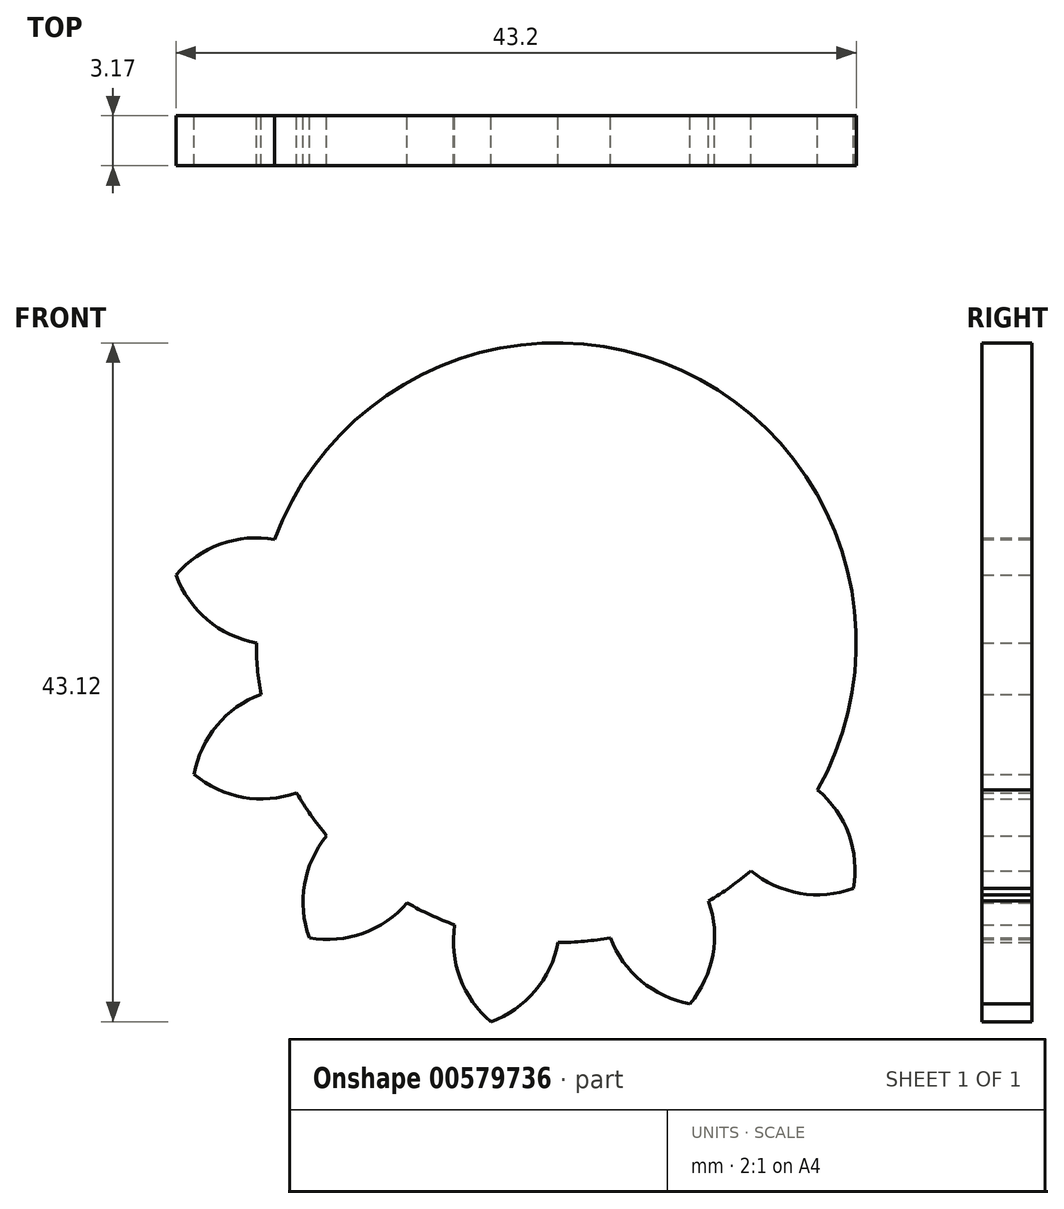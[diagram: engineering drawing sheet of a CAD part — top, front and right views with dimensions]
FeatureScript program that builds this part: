
annotation { "Feature Type Name" : "Feature", "Feature Type Description" : "" }
export const myFeature = defineFeature(function(context is Context, id is Id, definition is map)
    precondition{}
    {
        {
            var Q0;
            Q0=qCreatedBy(makeId("Front.planeOp"),FACE);
            var sketch = newSketch(context, id + "F0", { "sketchPlane" : qUnion([Q0])});
            skCircle(sketch, "E0", {"center": v(0, 0) * mm, "radius": 19.05 * mm});
            skArc(sketch, "E1", {"start": v(-17.89, 6.56) * mm, "mid": v(-21.32, 6.26) * mm, "end": v(-24.15, 4.29) * mm});
            skArc(sketch, "E2", {"start": v(-24.15, 4.29) * mm, "mid": v(-22.17, 1.46) * mm, "end": v(-19.05, 0) * mm});
            skArc(sketch, "E3.1.0", {"start": v(-18.71, -3.26) * mm, "mid": v(-21.54, -5.24) * mm, "end": v(-23, -8.36) * mm});
            skArc(sketch, "E3.1.1", {"start": v(-23, -8.36) * mm, "mid": v(-19.88, -9.82) * mm, "end": v(-16.44, -9.52) * mm});
            skArc(sketch, "E3.2.0", {"start": v(-14.52, -12.18) * mm, "mid": v(-15.98, -15.3) * mm, "end": v(-15.69, -18.74) * mm});
            skArc(sketch, "E3.2.1", {"start": v(-15.69, -18.74) * mm, "mid": v(-12.25, -18.44) * mm, "end": v(-9.42, -16.47) * mm});
            skArc(sketch, "E3.3.0", {"start": v(-6.43, -17.81) * mm, "mid": v(-6.13, -21.25) * mm, "end": v(-4.16, -24.07) * mm});
            skArc(sketch, "E3.3.1", {"start": v(-4.16, -24.07) * mm, "mid": v(-1.33, -22.1) * mm, "end": v(0.13, -18.98) * mm});
            skArc(sketch, "E3.4.0", {"start": v(3.39, -18.64) * mm, "mid": v(5.36, -21.47) * mm, "end": v(8.49, -22.93) * mm});
            skArc(sketch, "E3.4.1", {"start": v(8.49, -22.93) * mm, "mid": v(9.95, -19.8) * mm, "end": v(9.65, -16.37) * mm});
            skArc(sketch, "E3.5.0", {"start": v(12.3, -14.45) * mm, "mid": v(15.43, -15.9) * mm, "end": v(18.87, -15.61) * mm});
            skArc(sketch, "E3.5.1", {"start": v(18.87, -15.61) * mm, "mid": v(18.57, -12.18) * mm, "end": v(16.6, -9.35) * mm});
            skArc(sketch, "E3.6.0", {"start": v(17.94, -6.36) * mm, "mid": v(21.37, -6.06) * mm, "end": v(24.2, -4.09) * mm});
            skArc(sketch, "E3.6.1", {"start": v(24.2, -4.09) * mm, "mid": v(22.23, -1.26) * mm, "end": v(19.1, 0.2) * mm});
            skArc(sketch, "E3.7.0", {"start": v(18.77, 3.46) * mm, "mid": v(21.6, 5.44) * mm, "end": v(23.06, 8.56) * mm});
            skArc(sketch, "E3.7.1", {"start": v(23.06, 8.56) * mm, "mid": v(19.93, 10.02) * mm, "end": v(16.5, 9.73) * mm});
            skArc(sketch, "E3.8.0", {"start": v(14.58, 12.38) * mm, "mid": v(16.04, 15.5) * mm, "end": v(15.74, 18.94) * mm});
            skArc(sketch, "E3.8.1", {"start": v(15.74, 18.94) * mm, "mid": v(12.3, 18.65) * mm, "end": v(9.48, 16.67) * mm});
            skArc(sketch, "E3.9.0", {"start": v(6.48, 18.01) * mm, "mid": v(6.19, 21.45) * mm, "end": v(4.21, 24.28) * mm});
            skArc(sketch, "E3.9.1", {"start": v(4.21, 24.28) * mm, "mid": v(1.39, 22.3) * mm, "end": v(-0.07, 19.18) * mm});
            skArc(sketch, "E3.10.0", {"start": v(-3.34, 18.84) * mm, "mid": v(-5.31, 21.67) * mm, "end": v(-8.43, 23.13) * mm});
            skArc(sketch, "E3.10.1", {"start": v(-8.43, 23.13) * mm, "mid": v(-9.9, 20) * mm, "end": v(-9.6, 16.57) * mm});
            skArc(sketch, "E3.11.0", {"start": v(-12.26, 14.65) * mm, "mid": v(-15.38, 16.11) * mm, "end": v(-18.82, 15.81) * mm});
            skArc(sketch, "E3.11.1", {"start": v(-18.82, 15.81) * mm, "mid": v(-18.52, 12.38) * mm, "end": v(-16.54, 9.55) * mm});
            skPoint(sketch, "E3.center", {"position": v(0.03, 0.1) * mm});
            skSolve(sketch);
        }
        {
            var Q0;
            {var subQ0=sQuery(id+"F0.wireOp",EDGE,"E0");var subQ15=makeQuery(id+"F0.imprint","INTERSECT",VERTEX,{"derivedFrom":[subQ0,sQuery(id+"F0.wireOp",EDGE,"E3.6.1")]});Q0=makeQuery(id+"F0.imprint","IMPRINT",FACE,{"disambiguationData":[TD([[makeQuery(id+"F0.imprint","IMPRINT",EDGE,{"disambiguationData":[TD([[subQ15,-1.0]])],"derivedFrom":subQ0}),1.0]])]});}
            var Q1;
            {var subQ0=sQuery(id+"F0.wireOp",EDGE,"E3.9.0");Q1=makeQuery(id+"F0.imprint","IMPRINT",FACE,{"disambiguationData":[TD([[makeQuery(id+"F0.imprint","IMPRINT",EDGE,{"derivedFrom":subQ0}),1.0]])]});}
            var Q2;
            {var subQ0=sQuery(id+"F0.wireOp",EDGE,"E3.10.0");Q2=makeQuery(id+"F0.imprint","IMPRINT",FACE,{"disambiguationData":[TD([[makeQuery(id+"F0.imprint","IMPRINT",EDGE,{"derivedFrom":subQ0}),1.0]])]});}
            var Q3;
            {var subQ0=sQuery(id+"F0.wireOp",EDGE,"E3.11.0");Q3=makeQuery(id+"F0.imprint","IMPRINT",FACE,{"disambiguationData":[TD([[makeQuery(id+"F0.imprint","IMPRINT",EDGE,{"derivedFrom":subQ0}),1.0]])]});}
            var Q4;
            {var subQ0=sQuery(id+"F0.wireOp",EDGE,"E1");Q4=makeQuery(id+"F0.imprint","IMPRINT",FACE,{"disambiguationData":[TD([[makeQuery(id+"F0.imprint","IMPRINT",EDGE,{"derivedFrom":subQ0}),1.0]])]});}
            var Q5;
            {var subQ0=sQuery(id+"F0.wireOp",EDGE,"E3.1.0");Q5=makeQuery(id+"F0.imprint","IMPRINT",FACE,{"disambiguationData":[TD([[makeQuery(id+"F0.imprint","IMPRINT",EDGE,{"derivedFrom":subQ0}),1.0]])]});}
            var Q6;
            {var subQ0=sQuery(id+"F0.wireOp",EDGE,"E3.2.0");Q6=makeQuery(id+"F0.imprint","IMPRINT",FACE,{"disambiguationData":[TD([[makeQuery(id+"F0.imprint","IMPRINT",EDGE,{"derivedFrom":subQ0}),1.0]])]});}
            var Q7;
            {var subQ0=sQuery(id+"F0.wireOp",EDGE,"E3.3.0");Q7=makeQuery(id+"F0.imprint","IMPRINT",FACE,{"disambiguationData":[TD([[makeQuery(id+"F0.imprint","IMPRINT",EDGE,{"derivedFrom":subQ0}),1.0]])]});}
            var Q8;
            {var subQ0=sQuery(id+"F0.wireOp",EDGE,"E3.4.0");Q8=makeQuery(id+"F0.imprint","IMPRINT",FACE,{"disambiguationData":[TD([[makeQuery(id+"F0.imprint","IMPRINT",EDGE,{"derivedFrom":subQ0}),1.0]])]});}
            var Q9;
            {var subQ0=sQuery(id+"F0.wireOp",EDGE,"E3.5.0");Q9=makeQuery(id+"F0.imprint","IMPRINT",FACE,{"disambiguationData":[TD([[makeQuery(id+"F0.imprint","IMPRINT",EDGE,{"derivedFrom":subQ0}),1.0]])]});}
            var Q10;
            {var subQ0=sQuery(id+"F0.wireOp",EDGE,"E3.6.0");Q10=makeQuery(id+"F0.imprint","IMPRINT",FACE,{"disambiguationData":[TD([[makeQuery(id+"F0.imprint","IMPRINT",EDGE,{"derivedFrom":subQ0}),1.0]])]});}
            var Q11;
            {var subQ0=sQuery(id+"F0.wireOp",EDGE,"E3.7.0");Q11=makeQuery(id+"F0.imprint","IMPRINT",FACE,{"disambiguationData":[TD([[makeQuery(id+"F0.imprint","IMPRINT",EDGE,{"derivedFrom":subQ0}),1.0]])]});}
            var Q12;
            {var subQ0=sQuery(id+"F0.wireOp",EDGE,"E3.8.0");Q12=makeQuery(id+"F0.imprint","IMPRINT",FACE,{"disambiguationData":[TD([[makeQuery(id+"F0.imprint","IMPRINT",EDGE,{"derivedFrom":subQ0}),1.0]])]});}
            extrude(context, id + "F1", {"entities" : qUnion([Q0, Q1, Q2, Q3, Q4, Q5, Q6, Q7, Q8, Q9, Q10, Q11, Q12]), "depth" : 3.17 * mm, "offsetDistance" : 25.4 * mm});
        }
    });
